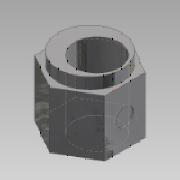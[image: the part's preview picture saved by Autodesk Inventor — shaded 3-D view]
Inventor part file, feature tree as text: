
AUTODESK INVENTOR PART (.ipt)
format: ipt  version: 2013 SP2 (Build 170200200, 200)  size: 125,440 bytes
history: native  units: mm
features: extrude x3, sketch x3
ambient origin geometry x8: Origin, YZ Plane, XZ Plane, XY Plane, X Axis, Y Axis, Z Axis, Center Point
bodies: Solid1 (feature_tree)
feature tree (6):
  extrude  "Extrusion1"  Depth=0.79mm
  extrude  "Extrusion2"  Depth=6.35mm TaperAngle=0.0deg
  extrude  "Extrusion3"  Depth=1.27mm TaperAngle=0.0deg
  sketch  "Sketch1"  dims[d0=7.87mm d1=0.79mm]
  sketch  "Sketch2"  dims[d2=5.0mm d3=6.35mm d4=0.0mm]
  sketch  "Sketch3"  dims[d5=7.11mm d6=1.27mm d7=0.0mm d8=2.0mm d9=0.15mm d10=0.0mm]
